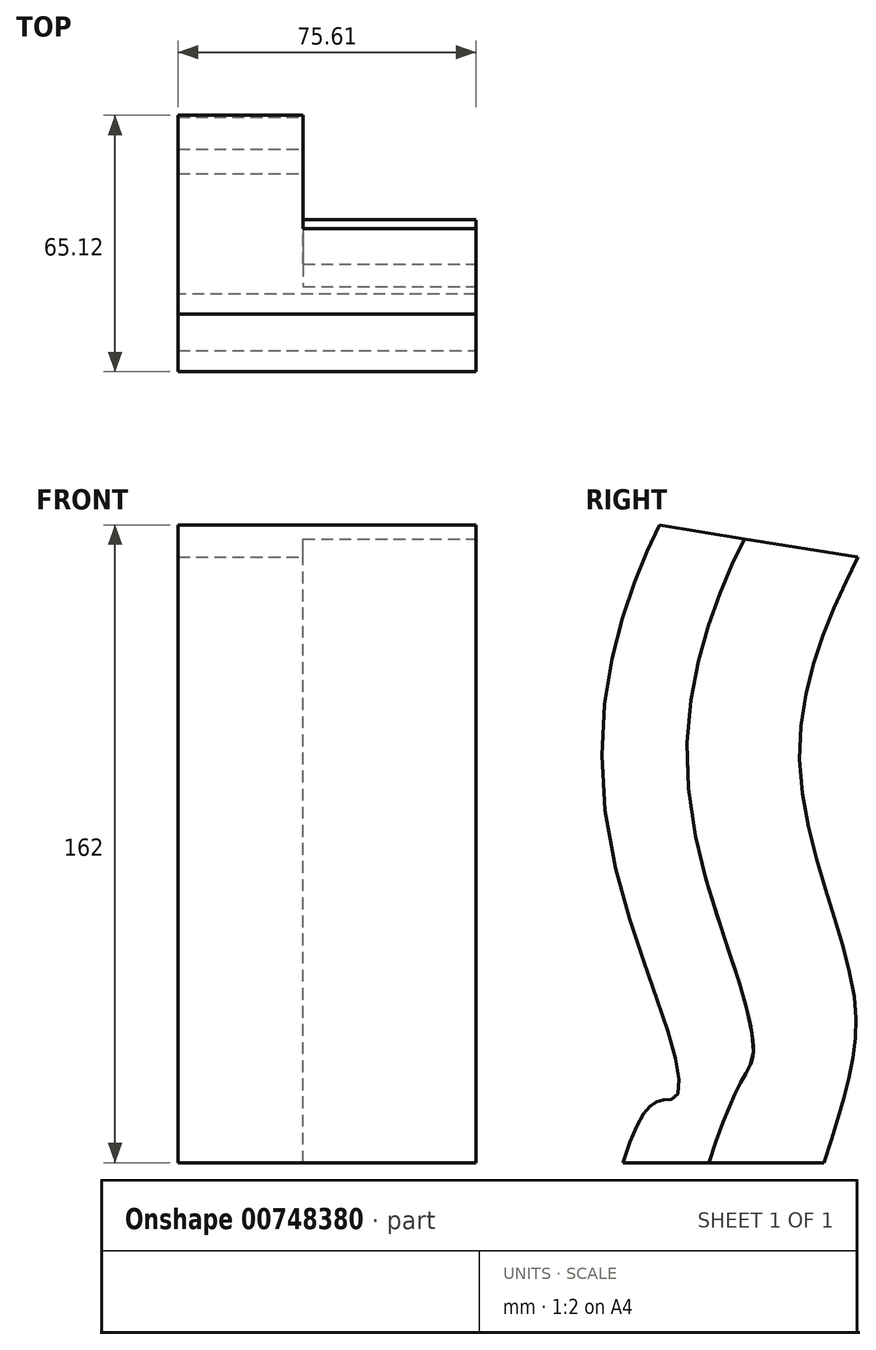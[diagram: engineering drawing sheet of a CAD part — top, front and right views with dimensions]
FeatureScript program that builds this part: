
annotation { "Feature Type Name" : "Feature", "Feature Type Description" : "" }
export const myFeature = defineFeature(function(context is Context, id is Id, definition is map)
    precondition{}
    {
        {
            var Q0;
            Q0=qCreatedBy(makeId("Top.planeOp"),FACE);
            var sketch = newSketch(context, id + "F0", { "sketchPlane" : qUnion([Q0])});
            skLineSegment(sketch, "E0.bottom", {"start": v(-45.11, 25.44) * mm, "end": v(-13.35, 25.44) * mm});
            skLineSegment(sketch, "E0.top", {"start": v(-45.11, -25.72) * mm, "end": v(-13.35, -25.72) * mm});
            skLineSegment(sketch, "E0.left", {"start": v(-45.11, 25.44) * mm, "end": v(-45.11, -25.72) * mm});
            skLineSegment(sketch, "E0.right", {"start": v(-13.35, 25.44) * mm, "end": v(-13.35, -3.8) * mm});
            skLineSegment(sketch, "E1.bottom", {"start": v(-13.35, -3.8) * mm, "end": v(30.5, -3.8) * mm});
            skLineSegment(sketch, "E1.top", {"start": v(-13.35, -25.72) * mm, "end": v(30.5, -25.72) * mm});
            skLineSegment(sketch, "E1.right", {"start": v(30.5, -3.8) * mm, "end": v(30.5, -25.72) * mm});
            skSolve(sketch);
        }
        {
            var Q0;
            Q0=qCreatedBy(makeId("Right.planeOp"),FACE);
            var sketch = newSketch(context, id + "F1", { "sketchPlane" : qUnion([Q0])});
            skFitSpline(sketch, "E2", {"points": [v(41.18, 0) * mm, v(47.92, 43.43) * mm, v(34.43, 101.89) * mm, v(49.6, 151.36) * mm], "startDerivative": vector(42.04, 135.03) * mm, "endDerivative": vector(71.16, 143.08) * mm});
            skSolve(sketch);
        }
        {
            var Q0;
            Q0=makeQuery(id+"F0.imprint","IMPRINT",FACE,{"disambiguationData":[TD([[makeQuery(id+"F0.imprint","IMPRINT",EDGE,{"derivedFrom":sQuery(id+"F0.wireOp",EDGE,"E0.bottom")}),-1.0]])]});
            var Q1;
            Q1=sQuery(id+"F1.wireOp",EDGE,"E2");
            sweep(context, id + "F2", {"profiles" : qUnion([Q0]), "path" : qUnion([Q1])});
        }
    });
